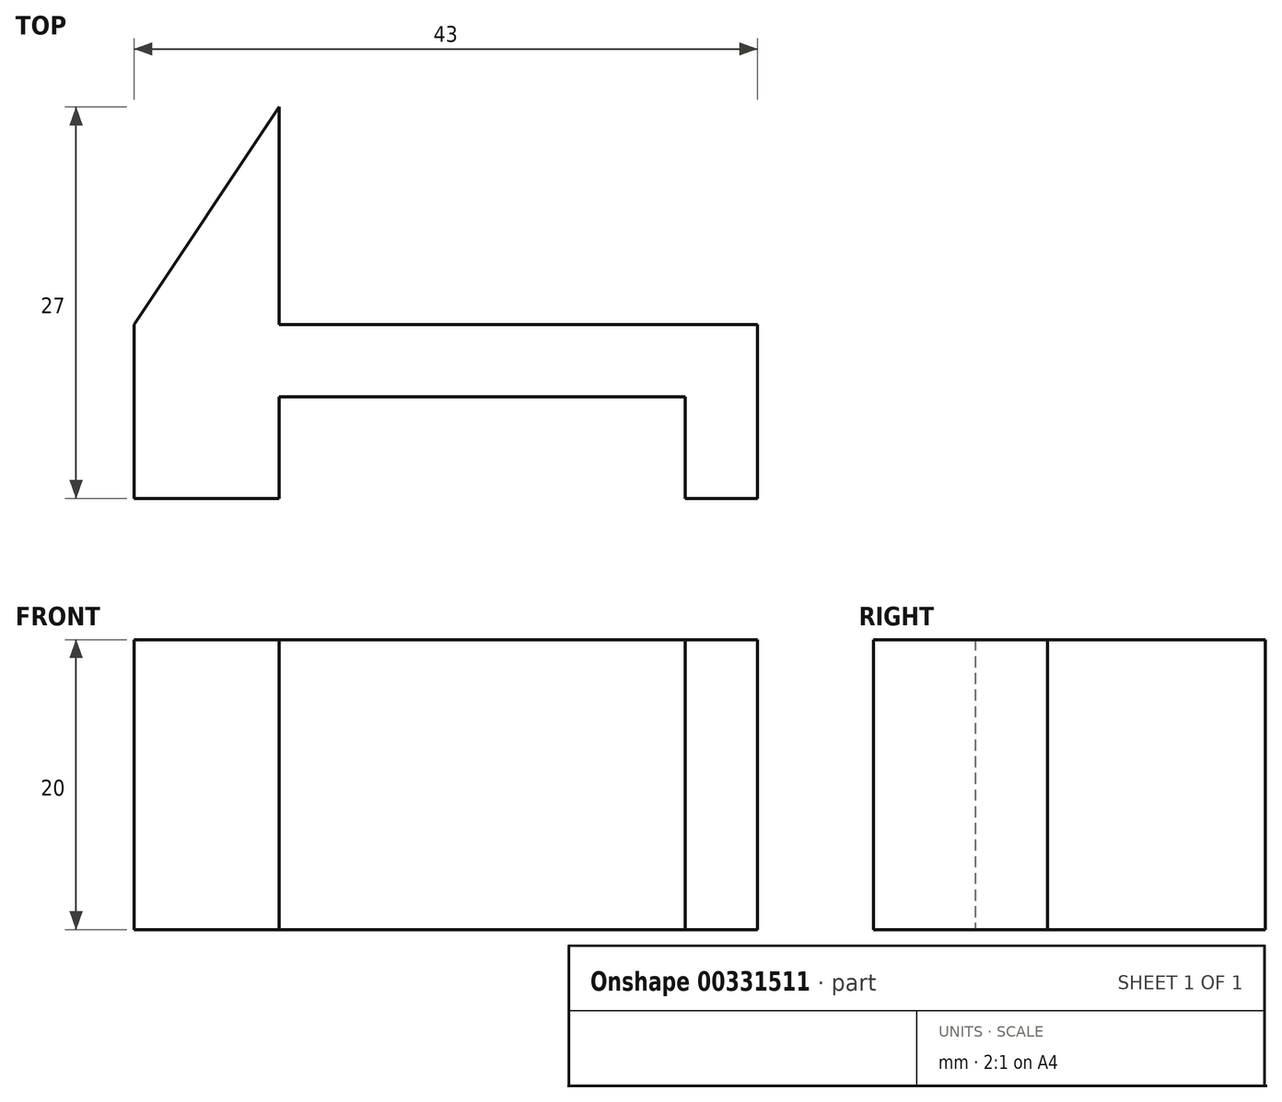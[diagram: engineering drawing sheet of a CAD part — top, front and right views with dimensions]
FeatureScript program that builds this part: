
annotation { "Feature Type Name" : "Feature", "Feature Type Description" : "" }
export const myFeature = defineFeature(function(context is Context, id is Id, definition is map)
    precondition{}
    {
        {
            var Q0;
            Q0=qCreatedBy(makeId("Top.planeOp"),FACE);
            var sketch = newSketch(context, id + "F0", { "sketchPlane" : qUnion([Q0])});
            skLineSegment(sketch, "E0", {"start": v(27.74, -2.28) * mm, "end": v(27.74, -9.28) * mm});
            skLineSegment(sketch, "E1", {"start": v(27.74, -9.28) * mm, "end": v(32.74, -9.28) * mm});
            skLineSegment(sketch, "E2", {"start": v(32.74, -9.28) * mm, "end": v(32.74, 2.72) * mm});
            skLineSegment(sketch, "E3", {"start": v(32.74, 2.72) * mm, "end": v(-0.26, 2.72) * mm});
            skLineSegment(sketch, "E4", {"start": v(-0.26, 2.72) * mm, "end": v(-0.26, 17.72) * mm});
            skLineSegment(sketch, "E5", {"start": v(-0.26, 17.72) * mm, "end": v(-10.26, 2.72) * mm});
            skLineSegment(sketch, "E6", {"start": v(-10.26, 2.72) * mm, "end": v(-10.26, -9.28) * mm});
            skLineSegment(sketch, "E7", {"start": v(-10.26, -9.28) * mm, "end": v(-0.26, -9.28) * mm});
            skLineSegment(sketch, "E8", {"start": v(-0.26, -9.28) * mm, "end": v(-0.26, -2.28) * mm});
            skLineSegment(sketch, "E9", {"start": v(-0.26, -2.28) * mm, "end": v(27.74, -2.28) * mm});
            skSolve(sketch);
        }
        {
            var Q0;
            Q0=makeQuery(id+"F0.imprint","IMPRINT",FACE,{"disambiguationData":[TD([[makeQuery(id+"F0.imprint","IMPRINT",EDGE,{"derivedFrom":sQuery(id+"F0.wireOp",EDGE,"E0")}),1.0]])]});
            extrude(context, id + "F1", {"entities" : qUnion([Q0]), "depth" : 20 * mm});
        }
    });
